# Revit family: Storage-Teknion-PCLG_Literatura_Glider_Shelf-R2015
name_source: partatom
category: Furniture
revit_build: Autodesk Revit Architecture 2015 (Build: 20140323_1530(x64)
units: mm (PartAtom-declared; Revit-internal decimal feet)

## types (2) — shared parameters
Assembly Code = E2020200
Default Elevation = 48 "
Manufacturer = Teknion
Manufacturer Fax = 416.661.4586
Part Number = PCLG
Product Documentation Link = https://d2r72yk5wmppdj.cloudfront.net
Product Line = Punt
Product Page URL = https://www.teknion.com
Series = Punt
Sustainability Data = http://www.teknion.com
URL = www.teknion.com
Unit Weight URL = http://www.teknion.com
Warranty = http://www.teknion.com

## per-type parameters (varying)
| type | 75" Top Shelves Visibility | Description | Height | Model |
| 75" High | Yes | Literatura Glider Shelf, 75" Height | 73.048 " | PCLG75 |
| 46" High | No | Literatura Glider Shelf, 46" Height | 44.505 " | PCLG46 |

## geometry (parser evidence)
native form markers: Sweep x2
no freeform markers — native parametric forms only
